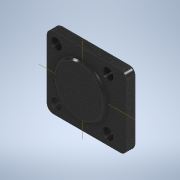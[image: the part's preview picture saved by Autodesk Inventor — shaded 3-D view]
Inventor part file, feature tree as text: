
AUTODESK INVENTOR PART (.ipt)
format: ipt  version: 2021.1 (Build 251245000, 245)  size: 169,472 bytes
history: native  units: in
note: dims shown in document units (in); Inventor stores cm internally (conversion verified against a paired STEP export)
features: extrude x2, sketch x1, chamfer x1, fillet x1
ambient origin geometry x8: Origin, YZ Plane, XZ Plane, XY Plane, X Axis, Y Axis, Z Axis, Center Point
bodies: Solid1 (feature_tree)
feature tree (5):
  sketch  "Sketch1"  dims[d0=5.0in d1=4.5in d2=2.2in d3=3.2in d4=4.6in d5=45.0deg d6=0.7in d7=1.5748in d9=360.0deg d11=0.4in d12=2.3326in d13=0.6in d14=0.0in d15=0.2in d16=0.0in d17=0.1in d18=0.125in d19=45.0deg d20=0.1in]
  extrude  "Extrusion1"  Depth=4.5in
  extrude  "Extrusion2"  Depth=0.1in
  chamfer  "Chamfer1"  Distance=3.2in
  fillet  "Fillet1"  Radius=4.6in
